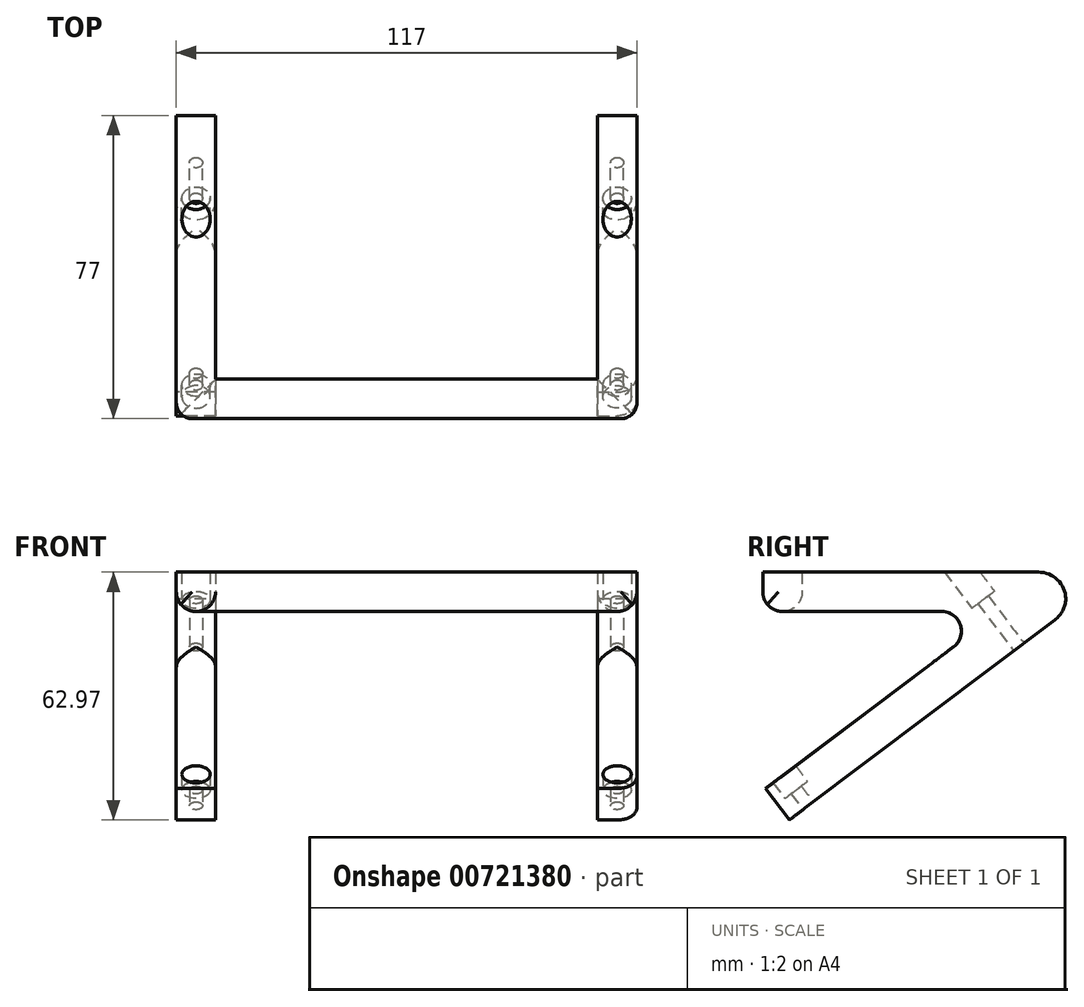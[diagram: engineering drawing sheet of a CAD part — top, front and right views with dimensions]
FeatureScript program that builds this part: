
annotation { "Feature Type Name" : "Feature", "Feature Type Description" : "" }
export const myFeature = defineFeature(function(context is Context, id is Id, definition is map)
    precondition{}
    {
        {
            var Q0;
            Q0=qCreatedBy(makeId("Top.planeOp"),FACE);
            var sketch = newSketch(context, id + "F0", { "sketchPlane" : qUnion([Q0])});
            skLineSegment(sketch, "E0.bottom", {"start": v(53.5, 33.5) * mm, "end": v(-53.5, 33.5) * mm});
            skLineSegment(sketch, "E0.top", {"start": v(53.5, -33.5) * mm, "end": v(-53.5, -33.5) * mm});
            skLineSegment(sketch, "E0.left", {"start": v(53.5, 33.5) * mm, "end": v(53.5, -33.5) * mm});
            skLineSegment(sketch, "E0.right", {"start": v(-53.5, 33.5) * mm, "end": v(-53.5, -33.5) * mm});
            skPoint(sketch, "E0.middle", {"position": v(0, 0) * mm});
            skSolve(sketch);
        }
        {
            var Q0;
            Q0=makeQuery(id+"F0.imprint","IMPRINT",FACE,{"disambiguationData":[TD([[makeQuery(id+"F0.imprint","IMPRINT",EDGE,{"derivedFrom":sQuery(id+"F0.wireOp",EDGE,"E0.bottom")}),1.0]])]});
            var sketch = newSketch(context, id + "F1", { "sketchPlane" : qUnion([Q0])});
            skLineSegment(sketch, "E1.0", {"start": v(-48.5, -28.5) * mm, "end": v(48.5, -28.5) * mm});
            skLineSegment(sketch, "E1.1", {"start": v(-48.5, 28.5) * mm, "end": v(-48.5, -28.5) * mm});
            skLineSegment(sketch, "E1.3", {"start": v(48.5, -28.5) * mm, "end": v(48.5, 28.5) * mm});
            skLineSegment(sketch, "E2.0", {"start": v(-58.5, -38.5) * mm, "end": v(58.5, -38.5) * mm});
            skLineSegment(sketch, "E2.1", {"start": v(-58.5, 38.5) * mm, "end": v(-58.5, -38.5) * mm});
            skLineSegment(sketch, "E2.2", {"start": v(58.5, 38.5) * mm, "end": v(48.5, 38.5) * mm});
            skLineSegment(sketch, "E2.3", {"start": v(58.5, -38.5) * mm, "end": v(58.5, 38.5) * mm});
            skLineSegment(sketch, "E3", {"start": v(-48.5, 28.5) * mm, "end": v(-48.5, 38.5) * mm});
            skLineSegment(sketch, "E4", {"start": v(48.5, 28.5) * mm, "end": v(48.5, 38.5) * mm});
            skLineSegment(sketch, "E5.trimOffspring", {"start": v(-48.5, 38.5) * mm, "end": v(-58.5, 38.5) * mm});
            skSolve(sketch);
        }
        {
            var Q0;
            Q0 = qSketchRegion(id + "F1", true);
            extrude(context, id + "F2", {"entities" : qUnion([Q0]), "depth" : 10 * mm, "offsetDistance" : 25 * mm});
        }
        {
            var Q0;
            Q0=makeQuery(id+"F2.opExtrude","SWEPT_FACE",FACE,{"disambiguationData":[OSD([sQuery(id+"F1.wireOp",EDGE,"E2.3")])]});
            var sketch = newSketch(context, id + "F3", { "sketchPlane" : qUnion([Q0])});
            skLineSegment(sketch, "E6", {"start": v(38.5, 0) * mm, "end": v(-31.77, -52.97) * mm});
            skLineSegment(sketch, "E7", {"start": v(-31.77, -52.97) * mm, "end": v(-37.79, -44.99) * mm});
            skLineSegment(sketch, "E8", {"start": v(-37.79, -44.99) * mm, "end": v(21.89, 0) * mm});
            skSolve(sketch);
        }
        {
            var Q0;
            {var subQ0=sQuery(id+"F3.wireOp",EDGE,"E6");Q0=makeQuery(id+"F3.imprint","IMPRINT",FACE,{"disambiguationData":[TD([[makeQuery(id+"F3.imprint","IMPRINT",EDGE,{"derivedFrom":subQ0}),-1.0]])]});}
            extrude(context, id + "F4", {"entities" : qUnion([Q0]), "operationType" : NewBodyOperationType.ADD, "oppositeDirection" : true, "depth" : 10 * mm, "offsetDistance" : 25 * mm});
        }
        {
            var Q0;
            Q0=makeQuery(id+"F2.opExtrude","SWEPT_FACE",FACE,{"disambiguationData":[OSD([sQuery(id+"F1.wireOp",EDGE,"E2.1")])]});
            var sketch = newSketch(context, id + "F5", { "sketchPlane" : qUnion([Q0])});
            skLineSegment(sketch, "E9", {"start": v(-38.5, 0) * mm, "end": v(31.77, -52.97) * mm});
            skLineSegment(sketch, "E10", {"start": v(31.77, -52.97) * mm, "end": v(37.79, -44.99) * mm});
            skLineSegment(sketch, "E11", {"start": v(37.79, -44.99) * mm, "end": v(-21.89, 0) * mm});
            skSolve(sketch);
        }
        {
            var Q0;
            {var subQ0=sQuery(id+"F5.wireOp",EDGE,"E9");Q0=makeQuery(id+"F5.imprint","IMPRINT",FACE,{"disambiguationData":[TD([[makeQuery(id+"F5.imprint","IMPRINT",EDGE,{"derivedFrom":subQ0}),1.0]])]});}
            extrude(context, id + "F6", {"entities" : qUnion([Q0]), "operationType" : NewBodyOperationType.ADD, "oppositeDirection" : true, "depth" : 10 * mm, "offsetDistance" : 25 * mm});
        }
        {
            var Q0;
            Q0=makeQuery(id+"F2.opExtrude","CAP_FACE",FACE,{"disambiguationData":[OSD([sQuery(id+"F1.wireOp",EDGE,"E1.0"),sQuery(id+"F1.wireOp",EDGE,"E1.1"),sQuery(id+"F1.wireOp",EDGE,"E1.3"),sQuery(id+"F1.wireOp",EDGE,"E2.0"),sQuery(id+"F1.wireOp",EDGE,"E2.1"),sQuery(id+"F1.wireOp",EDGE,"E2.2"),sQuery(id+"F1.wireOp",EDGE,"E2.3"),sQuery(id+"F1.wireOp",EDGE,"E3"),sQuery(id+"F1.wireOp",EDGE,"E4"),sQuery(id+"F1.wireOp",EDGE,"E5.trimOffspring")])],"isStart":true});
            fillet(context, id + "F7", {"entities" : qUnion([Q0]), "radius" : 5 * mm, "tangentPropagation" : true, "allowEdgeOverflow" : false});
        }
        {
            var Q0;
            Q0=makeQuery(id+"F2.opExtrude","CAP_EDGE",EDGE,{"disambiguationData":[OSD([sQuery(id+"F1.wireOp",EDGE,"E5.trimOffspring")])],"isStart":false});
            var Q1;
            Q1=makeQuery(id+"F2.opExtrude","CAP_EDGE",EDGE,{"disambiguationData":[OSD([sQuery(id+"F1.wireOp",EDGE,"E2.2")])],"isStart":false});
            var Q2;
            {var subQ0=sQuery(id+"F1.wireOp",EDGE,"E5.trimOffspring");Q2=makeQuery(id+"F6.boolean.opBoolean","MERGE",EDGE,{"derivedFrom":[makeQuery(id+"F2.opExtrude","CAP_EDGE",EDGE,{"disambiguationData":[OSD([subQ0])],"isStart":true}),makeQuery(id+"F6.opExtrude","SWEPT_EDGE",EDGE,{"disambiguationData":[OSD([sQuery(id+"F1.wireOp",EDGE,"E2.1"),subQ0,sQuery(id+"F5.wireOp",EDGE,"E9")])]})]});}
            var Q3;
            {var subQ0=sQuery(id+"F1.wireOp",EDGE,"E2.2");Q3=makeQuery(id+"F4.boolean.opBoolean","MERGE",EDGE,{"derivedFrom":[makeQuery(id+"F2.opExtrude","CAP_EDGE",EDGE,{"disambiguationData":[OSD([subQ0])],"isStart":true}),makeQuery(id+"F4.opExtrude","SWEPT_EDGE",EDGE,{"disambiguationData":[OSD([subQ0,sQuery(id+"F1.wireOp",EDGE,"E2.3"),sQuery(id+"F3.wireOp",EDGE,"E6")])]})]});}
            fillet(context, id + "F8", {"entities" : qUnion([Q0, Q1, Q2, Q3]), "radius" : 7 * mm, "tangentPropagation" : true, "allowEdgeOverflow" : false});
        }
        {
            var Q0;
            Q0=makeQuery(id+"F6.opExtrude","SWEPT_FACE",FACE,{"disambiguationData":[OSD([sQuery(id+"F5.wireOp",EDGE,"E9")])]});
            var sketch = newSketch(context, id + "F9", { "sketchPlane" : qUnion([Q0])});
            skLineSegment(sketch, "E12", {"start": v(-53.5, 57.26) * mm, "end": v(-53.5, -27.25) * mm, "construction": true});
            skCircle(sketch, "E13", {"center": v(-53.5, 51.26) * mm, "radius": 1.65 * mm});
            skCircle(sketch, "E14", {"center": v(-53.5, -15.74) * mm, "radius": 1.65 * mm});
            skSolve(sketch);
        }
        {
            var Q0;
            Q0=makeQuery(id+"F7.opFillet","BLEND_EDGE",EDGE,{"blendedFrom":[makeQuery(id+"F6.opExtrude","CAP_EDGE",EDGE,{"disambiguationData":[OSD([sQuery(id+"F5.wireOp",EDGE,"E11")])],"isStart":false}),makeQuery(id+"F6.opExtrude","SWEPT_FACE",FACE,{"disambiguationData":[OSD([sQuery(id+"F5.wireOp",EDGE,"E10")])]})],"blendedInto":[makeQuery(id+"F6.opExtrude","SWEPT_FACE",FACE,{"disambiguationData":[OSD([sQuery(id+"F5.wireOp",EDGE,"E10")])]})]});
            var Q1;
            Q1=makeQuery(id+"F4.opExtrude","CAP_EDGE",EDGE,{"disambiguationData":[OSD([sQuery(id+"F3.wireOp",EDGE,"E7")])],"isStart":true});
            fillet(context, id + "F10", {"entities" : qUnion([Q0, Q1]), "radius" : 5 * mm, "tangentPropagation" : true, "allowEdgeOverflow" : false});
        }
        {
            var Q0;
            Q0=makeQuery(id+"F2.opExtrude","SWEPT_EDGE",EDGE,{"disambiguationData":[OSD([sQuery(id+"F1.wireOp",EDGE,"E2.0"),sQuery(id+"F1.wireOp",EDGE,"E2.1")])]});
            var Q1;
            Q1=makeQuery(id+"F2.opExtrude","SWEPT_EDGE",EDGE,{"disambiguationData":[OSD([sQuery(id+"F1.wireOp",EDGE,"E2.0"),sQuery(id+"F1.wireOp",EDGE,"E2.3")])]});
            fillet(context, id + "F11", {"entities" : qUnion([Q0, Q1]), "radius" : 4 * mm, "tangentPropagation" : true, "allowEdgeOverflow" : false});
        }
        {
            var Q0;
            Q0=makeQuery(id+"F4.opExtrude","SWEPT_FACE",FACE,{"disambiguationData":[OSD([sQuery(id+"F3.wireOp",EDGE,"E6")])]});
            var sketch = newSketch(context, id + "F12", { "sketchPlane" : qUnion([Q0])});
            skCircle(sketch, "E15", {"center": v(53.5, 51.26) * mm, "radius": 1.65 * mm});
            skPoint(sketch, "E15.centerSnap0", {"position": v(53.5, 57.26) * mm});
            skCircle(sketch, "E16", {"center": v(53.5, -15.74) * mm, "radius": 1.65 * mm});
            skPoint(sketch, "E16.centerSnap0", {"position": v(53.5, -27.25) * mm});
            skSolve(sketch);
        }
        {
            var Q0;
            Q0=makeQuery(id+"F9.imprint","IMPRINT",FACE,{"disambiguationData":[TD([[makeQuery(id+"F9.imprint","IMPRINT",EDGE,{"derivedFrom":sQuery(id+"F9.wireOp",EDGE,"E13")}),1.0]])]});
            var Q1;
            Q1=makeQuery(id+"F9.imprint","IMPRINT",FACE,{"disambiguationData":[TD([[makeQuery(id+"F9.imprint","IMPRINT",EDGE,{"derivedFrom":sQuery(id+"F9.wireOp",EDGE,"E14")}),1.0]])]});
            var Q2;
            Q2=makeQuery(id+"F12.imprint","IMPRINT",FACE,{"disambiguationData":[TD([[makeQuery(id+"F12.imprint","IMPRINT",EDGE,{"derivedFrom":sQuery(id+"F12.wireOp",EDGE,"E16")}),1.0]])]});
            var Q3;
            Q3=makeQuery(id+"F12.imprint","IMPRINT",FACE,{"disambiguationData":[TD([[makeQuery(id+"F12.imprint","IMPRINT",EDGE,{"derivedFrom":sQuery(id+"F12.wireOp",EDGE,"E15")}),1.0]])]});
            var Q4;
            Q4=sQuery(id+"F9.wireOp",EDGE,"E13");
            var Q5;
            Q5=sQuery(id+"F12.wireOp",EDGE,"E15");
            var Q6;
            Q6=sQuery(id+"F12.wireOp",EDGE,"E16");
            var Q7;
            Q7=sQuery(id+"F9.wireOp",EDGE,"E14");
            extrude(context, id + "F13", {"entities" : qUnion([Q0, Q1, Q2, Q3]), "operationType" : NewBodyOperationType.REMOVE, "surfaceEntities" : qUnion([Q4, Q5, Q6, Q7]), "oppositeDirection" : true, "depth" : 27 * mm, "offsetDistance" : 25 * mm});
        }
        {
            var Q0;
            Q0=makeQuery(id+"F6.opExtrude","SWEPT_FACE",FACE,{"disambiguationData":[OSD([sQuery(id+"F5.wireOp",EDGE,"E9")])]});
            var sketch = newSketch(context, id + "F14", { "sketchPlane" : qUnion([Q0])});
            skCircle(sketch, "E17", {"center": v(-53.5, -15.74) * mm, "radius": 3.6 * mm});
            skSolve(sketch);
        }
        {
            var Q0;
            Q0=makeQuery(id+"F14.imprint","IMPRINT",FACE,{"disambiguationData":[TD([[makeQuery(id+"F14.imprint","IMPRINT",EDGE,{"derivedFrom":sQuery(id+"F14.wireOp",EDGE,"E17")}),1.0]])]});
            var Q1;
            Q1=sQuery(id+"F14.wireOp",EDGE,"E17");
            extrude(context, id + "F15", {"entities" : qUnion([Q0]), "operationType" : NewBodyOperationType.REMOVE, "surfaceEntities" : qUnion([Q1]), "oppositeDirection" : true, "depth" : 29.2 * mm, "offsetDistance" : 25 * mm, "hasSecondDirection" : true, "secondDirectionOppositeDirection" : true, "secondDirectionDepth" : 15 * mm});
        }
        {
            var Q0;
            Q0=makeQuery(id+"F4.opExtrude","SWEPT_FACE",FACE,{"disambiguationData":[OSD([sQuery(id+"F3.wireOp",EDGE,"E6")])]});
            var sketch = newSketch(context, id + "F16", { "sketchPlane" : qUnion([Q0])});
            skCircle(sketch, "E18", {"center": v(53.5, -15.74) * mm, "radius": 3.6 * mm});
            skSolve(sketch);
        }
        {
            var Q0;
            Q0=makeQuery(id+"F16.imprint","IMPRINT",FACE,{"disambiguationData":[TD([[makeQuery(id+"F16.imprint","IMPRINT",EDGE,{"derivedFrom":sQuery(id+"F16.wireOp",EDGE,"E18")}),1.0]])]});
            extrude(context, id + "F17", {"entities" : qUnion([Q0]), "operationType" : NewBodyOperationType.REMOVE, "oppositeDirection" : true, "depth" : 28 * mm, "offsetDistance" : 25 * mm, "hasSecondDirection" : true, "secondDirectionOppositeDirection" : true, "secondDirectionDepth" : 15 * mm});
        }
        {
            var Q0;
            Q0=makeQuery(id+"F4.opExtrude","SWEPT_FACE",FACE,{"disambiguationData":[OSD([sQuery(id+"F3.wireOp",EDGE,"E6")])]});
            var sketch = newSketch(context, id + "F18", { "sketchPlane" : qUnion([Q0])});
            skCircle(sketch, "E19", {"center": v(53.5, 51.26) * mm, "radius": 3.6 * mm});
            skSolve(sketch);
        }
        {
            var Q0;
            Q0=makeQuery(id+"F18.imprint","IMPRINT",FACE,{"disambiguationData":[TD([[makeQuery(id+"F18.imprint","IMPRINT",EDGE,{"derivedFrom":sQuery(id+"F18.wireOp",EDGE,"E19")}),1.0]])]});
            extrude(context, id + "F19", {"entities" : qUnion([Q0]), "operationType" : NewBodyOperationType.REMOVE, "oppositeDirection" : true, "depth" : 16.1 * mm, "offsetDistance" : 25 * mm, "hasSecondDirection" : true, "secondDirectionOppositeDirection" : true, "secondDirectionDepth" : 5 * mm});
        }
        {
            var Q0;
            Q0=makeQuery(id+"F6.opExtrude","SWEPT_FACE",FACE,{"disambiguationData":[OSD([sQuery(id+"F5.wireOp",EDGE,"E9")])]});
            var sketch = newSketch(context, id + "F20", { "sketchPlane" : qUnion([Q0])});
            skCircle(sketch, "E20", {"center": v(-53.5, 51.26) * mm, "radius": 3.6 * mm});
            skSolve(sketch);
        }
        {
            var Q0;
            Q0=makeQuery(id+"F20.imprint","IMPRINT",FACE,{"disambiguationData":[TD([[makeQuery(id+"F20.imprint","IMPRINT",EDGE,{"derivedFrom":sQuery(id+"F20.wireOp",EDGE,"E20")}),1.0]])]});
            extrude(context, id + "F21", {"entities" : qUnion([Q0]), "operationType" : NewBodyOperationType.REMOVE, "oppositeDirection" : true, "depth" : 16 * mm, "offsetDistance" : 25 * mm, "hasSecondDirection" : true, "secondDirectionOppositeDirection" : true, "secondDirectionDepth" : 5 * mm});
        }
    });
